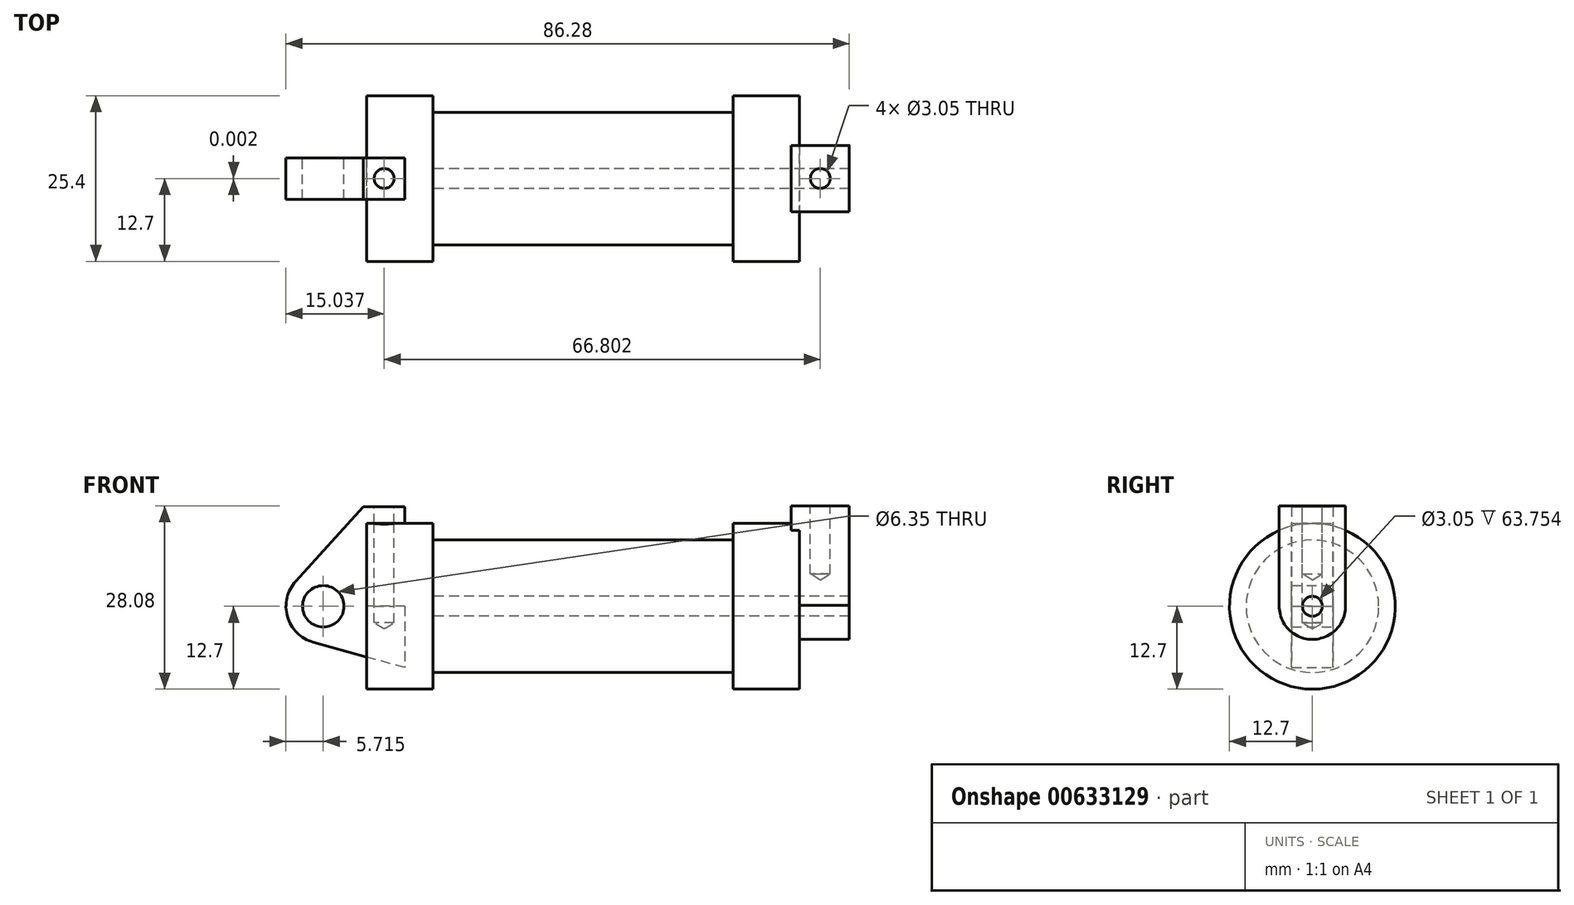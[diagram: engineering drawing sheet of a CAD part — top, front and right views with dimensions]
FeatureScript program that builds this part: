
annotation { "Feature Type Name" : "Feature", "Feature Type Description" : "" }
export const myFeature = defineFeature(function(context is Context, id is Id, definition is map)
    precondition{}
    {
        {
            var Q0;
            Q0=qCreatedBy(makeId("Front.planeOp"),FACE);
            var sketch = newSketch(context, id + "F0", { "sketchPlane" : qUnion([Q0])});
            skLineSegment(sketch, "E0", {"start": v(0, 0) * mm, "end": v(0, 12.7) * mm});
            skLineSegment(sketch, "E1", {"start": v(0, 12.7) * mm, "end": v(10.16, 12.7) * mm});
            skLineSegment(sketch, "E2", {"start": v(10.16, 12.7) * mm, "end": v(10.16, 10.16) * mm});
            skLineSegment(sketch, "E3", {"start": v(10.16, 10.16) * mm, "end": v(56.13, 10.16) * mm});
            skLineSegment(sketch, "E4", {"start": v(56.13, 10.16) * mm, "end": v(56.13, 12.7) * mm});
            skLineSegment(sketch, "E5", {"start": v(56.13, 12.7) * mm, "end": v(66.3, 12.7) * mm});
            skLineSegment(sketch, "E6", {"start": v(66.3, 12.7) * mm, "end": v(66.3, 0) * mm});
            skLineSegment(sketch, "E7", {"start": v(66.3, 0) * mm, "end": v(0, 0) * mm});
            skLineSegment(sketch, "E8", {"start": v(5.84, 15.24) * mm, "end": v(-0.5, 15.24) * mm});
            skLineSegment(sketch, "E9", {"start": v(-0.5, 15.24) * mm, "end": v(-10.88, 3.85) * mm});
            skLineSegment(sketch, "E10", {"start": v(0, 0) * mm, "end": v(-6.65, 0) * mm});
            skCircle(sketch, "E11", {"center": v(-6.65, 0) * mm, "radius": 5.72 * mm});
            skCircle(sketch, "E12", {"center": v(-6.65, 0) * mm, "radius": 3.18 * mm});
            skLineSegment(sketch, "E13", {"start": v(5.84, 15.24) * mm, "end": v(5.84, -9.4) * mm});
            skLineSegment(sketch, "E14", {"start": v(5.84, -9.4) * mm, "end": v(-8.18, -5.5) * mm});
            skSolve(sketch);
        }
        {
            var Q0;
            {var subQ0=sQuery(id+"F0.wireOp",EDGE,"E2");Q0=makeQuery(id+"F0.imprint","IMPRINT",FACE,{"disambiguationData":[TD([[makeQuery(id+"F0.imprint","IMPRINT",EDGE,{"derivedFrom":subQ0}),-1.0]])]});}
            var Q1;
            {var subQ0=sQuery(id+"F0.wireOp",EDGE,"E0");Q1=makeQuery(id+"F0.imprint","IMPRINT",FACE,{"disambiguationData":[TD([[makeQuery(id+"F0.imprint","IMPRINT",EDGE,{"derivedFrom":subQ0}),-1.0]])]});}
            var Q2;
            Q2=sQuery(id+"F0.wireOp",EDGE,"E7");
            revolve(context, id + "F1", {"entities" : qUnion([Q0, Q1]), "axis" : qUnion([Q2]), "revolveType" : RevolveType.FULL});
        }
        {
            var Q0;
            {var subQ0=sQuery(id+"F0.wireOp",EDGE,"E14");Q0=makeQuery(id+"F0.imprint","IMPRINT",FACE,{"disambiguationData":[TD([[makeQuery(id+"F0.imprint","IMPRINT",EDGE,{"derivedFrom":subQ0}),-1.0]])]});}
            var Q1;
            {var subQ1=sQuery(id+"F0.wireOp",EDGE,"E0");Q1=makeQuery(id+"F0.imprint","IMPRINT",FACE,{"disambiguationData":[TD([[makeQuery(id+"F0.imprint","IMPRINT",EDGE,{"derivedFrom":subQ1}),1.0]])]});}
            var Q2;
            {var subQ5=sQuery(id+"F0.wireOp",EDGE,"E12");Q2=makeQuery(id+"F0.imprint","IMPRINT",FACE,{"disambiguationData":[TD([[makeQuery(id+"F0.imprint","IMPRINT",EDGE,{"derivedFrom":subQ5}),-1.0]])]});}
            extrude(context, id + "F2", {"entities" : qUnion([Q0, Q1, Q2]), "endBound" : BoundingType.SYMMETRIC, "depth" : 6.35 * mm, "offsetDistance" : 25.4 * mm});
        }
        {
            var Q0;
            Q0=makeQuery(id+"F1.opRevolve","SWEPT_FACE",FACE,{"disambiguationData":[OSD([sQuery(id+"F0.wireOp",EDGE,"E6")])]});
            var sketch = newSketch(context, id + "F3", { "sketchPlane" : qUnion([Q0])});
            skCircle(sketch, "E15", {"center": v(0, 0) * mm, "radius": 1.52 * mm});
            skCircle(sketch, "E16", {"center": v(0, 0) * mm, "radius": 5.08 * mm});
            skLineSegment(sketch, "E17", {"start": v(5.08, 0.14) * mm, "end": v(5.08, 15.38) * mm});
            skLineSegment(sketch, "E18", {"start": v(-5.08, 0.14) * mm, "end": v(-5.08, 15.38) * mm});
            skLineSegment(sketch, "E19", {"start": v(-5.08, 15.38) * mm, "end": v(5.08, 15.38) * mm});
            skSolve(sketch);
        }
        {
            var Q0;
            Q0=makeQuery(id+"F3.imprint","IMPRINT",FACE,{"disambiguationData":[TD([[makeQuery(id+"F3.imprint","IMPRINT",EDGE,{"derivedFrom":sQuery(id+"F3.wireOp",EDGE,"E15")}),-1.0]])]});
            var Q1;
            {var subQ0=sQuery(id+"F3.wireOp",EDGE,"E17");var subQ1=sQuery(id+"F3.wireOp",EDGE,"E16");var subQ2=makeQuery(id+"F3.imprint","INTERSECT",VERTEX,{"derivedFrom":[subQ1,subQ0]});Q1=makeQuery(id+"F3.imprint","IMPRINT",FACE,{"disambiguationData":[TD([[makeQuery(id+"F3.imprint","IMPRINT",EDGE,{"disambiguationData":[TD([[subQ2,-1.0]])],"derivedFrom":subQ1}),-1.0]])]});}
            var Q2;
            {var subQ0=sQuery(id+"F3.wireOp",EDGE,"E19");Q2=makeQuery(id+"F3.imprint","IMPRINT",FACE,{"disambiguationData":[TD([[makeQuery(id+"F3.imprint","IMPRINT",EDGE,{"derivedFrom":subQ0}),-1.0]])]});}
            extrude(context, id + "F4", {"entities" : qUnion([Q0, Q1, Q2]), "operationType" : NewBodyOperationType.ADD, "depth" : 7.62 * mm, "offsetDistance" : 25.4 * mm, "hasSecondDirection" : true, "secondDirectionOppositeDirection" : true, "secondDirectionDepth" : 1.27 * mm});
        }
        {
            var Q0;
            Q0=makeQuery(id+"F4.boolean.opBoolean","SPLIT",FACE,{"disambiguationData":[TD([makeQuery(id+"F4.opExtrude","SWEPT_FACE",FACE,{"disambiguationData":[OSD([sQuery(id+"F3.wireOp",EDGE,"E15")])]})])],"derivedFrom":makeQuery(id+"F1.opRevolve","SWEPT_FACE",FACE,{"disambiguationData":[OSD([sQuery(id+"F0.wireOp",EDGE,"E6")])]})});
            var Q1;
            Q1=makeQuery(id+"F1.opRevolve","SWEPT_FACE",FACE,{"disambiguationData":[OSD([sQuery(id+"F0.wireOp",EDGE,"E2")])]});
            extrude(context, id + "F5", {"entities" : qUnion([Q0]), "operationType" : NewBodyOperationType.REMOVE, "endBound" : BoundingType.UP_TO_SURFACE, "oppositeDirection" : true, "depth" : 25.4 * mm, "endBoundEntityFace" : qUnion([Q1]), "offsetDistance" : 25.4 * mm});
        }
        {
            var Q0;
            Q0=makeQuery(id+"F4.opExtrude","SWEPT_FACE",FACE,{"disambiguationData":[OSD([sQuery(id+"F3.wireOp",EDGE,"E19")])]});
            var sketch = newSketch(context, id + "F6", { "sketchPlane" : qUnion([Q0])});
            skCircle(sketch, "E20", {"center": v(69.47, 0) * mm, "radius": 1.52 * mm});
            skPoint(sketch, "E20.centerSnap0", {"position": v(69.47, -5.07) * mm});
            skPoint(sketch, "E20.centerSnap1", {"position": v(65.02, 0) * mm});
            skSolve(sketch);
        }
        {
            var Q0;
            Q0=sQuery(id+"F6.wireOp",VERTEX,"E20.center");
            var Q1;
            Q1=makeQuery(id+"F1.opRevolve","SWEPT_BODY",BODY,{"disambiguationData":[OSD([sQuery(id+"F0.wireOp",EDGE,"E0"),sQuery(id+"F0.wireOp",EDGE,"E1"),sQuery(id+"F0.wireOp",EDGE,"E2"),sQuery(id+"F0.wireOp",EDGE,"E3"),sQuery(id+"F0.wireOp",EDGE,"E4"),sQuery(id+"F0.wireOp",EDGE,"E5"),sQuery(id+"F0.wireOp",EDGE,"E6"),sQuery(id+"F0.wireOp",EDGE,"E7")])]});
            hole(context, id + "F7", {"style" : HoleStyle.SIMPLE, "endStyle" : HoleEndStyle.BLIND, "holeDiameter" : 3.05 * mm, "majorDiameter" : 6.35 * mm, "holeDepth" : 10.4 * mm, "isTappedThrough" : true, "tappedDepth" : 12.7 * mm, "tapClearance" : 3, "locations" : qUnion([Q0]), "scope" : qUnion([Q1])});
        }
        {
            var Q0;
            Q0=makeQuery(id+"F2.opExtrude","SWEPT_FACE",FACE,{"disambiguationData":[OSD([sQuery(id+"F0.wireOp",EDGE,"E8")])]});
            var sketch = newSketch(context, id + "F8", { "sketchPlane" : qUnion([Q0])});
            skCircle(sketch, "E21", {"center": v(2.67, 0) * mm, "radius": 1.52 * mm});
            skPoint(sketch, "E21.centerSnap0", {"position": v(5.84, 0) * mm});
            skPoint(sketch, "E21.centerSnap1", {"position": v(2.67, -3.18) * mm});
            skSolve(sketch);
        }
        {
            var Q0;
            Q0=sQuery(id+"F8.wireOp",VERTEX,"E21.center");
            var Q1;
            Q1=makeQuery(id+"F1.opRevolve","SWEPT_BODY",BODY,{"disambiguationData":[OSD([sQuery(id+"F0.wireOp",EDGE,"E0"),sQuery(id+"F0.wireOp",EDGE,"E1"),sQuery(id+"F0.wireOp",EDGE,"E2"),sQuery(id+"F0.wireOp",EDGE,"E3"),sQuery(id+"F0.wireOp",EDGE,"E4"),sQuery(id+"F0.wireOp",EDGE,"E5"),sQuery(id+"F0.wireOp",EDGE,"E6"),sQuery(id+"F0.wireOp",EDGE,"E7")])]});
            var Q2;
            Q2=makeQuery(id+"F2.opExtrude","SWEPT_BODY",BODY,{"disambiguationData":[OSD([sQuery(id+"F0.wireOp",EDGE,"E0"),sQuery(id+"F0.wireOp",EDGE,"E1"),sQuery(id+"F0.wireOp",EDGE,"E7"),sQuery(id+"F0.wireOp",EDGE,"E8"),sQuery(id+"F0.wireOp",EDGE,"E9"),sQuery(id+"F0.wireOp",EDGE,"E11"),sQuery(id+"F0.wireOp",EDGE,"E12"),sQuery(id+"F0.wireOp",EDGE,"E13"),sQuery(id+"F0.wireOp",EDGE,"E14")])]});
            hole(context, id + "F9", {"style" : HoleStyle.SIMPLE, "endStyle" : HoleEndStyle.BLIND, "holeDiameter" : 3.05 * mm, "majorDiameter" : 6.35 * mm, "holeDepth" : 17.78 * mm, "isTappedThrough" : true, "tappedDepth" : 12.7 * mm, "tapClearance" : 3, "locations" : qUnion([Q0]), "scope" : qUnion([Q1, Q2])});
        }
    });
